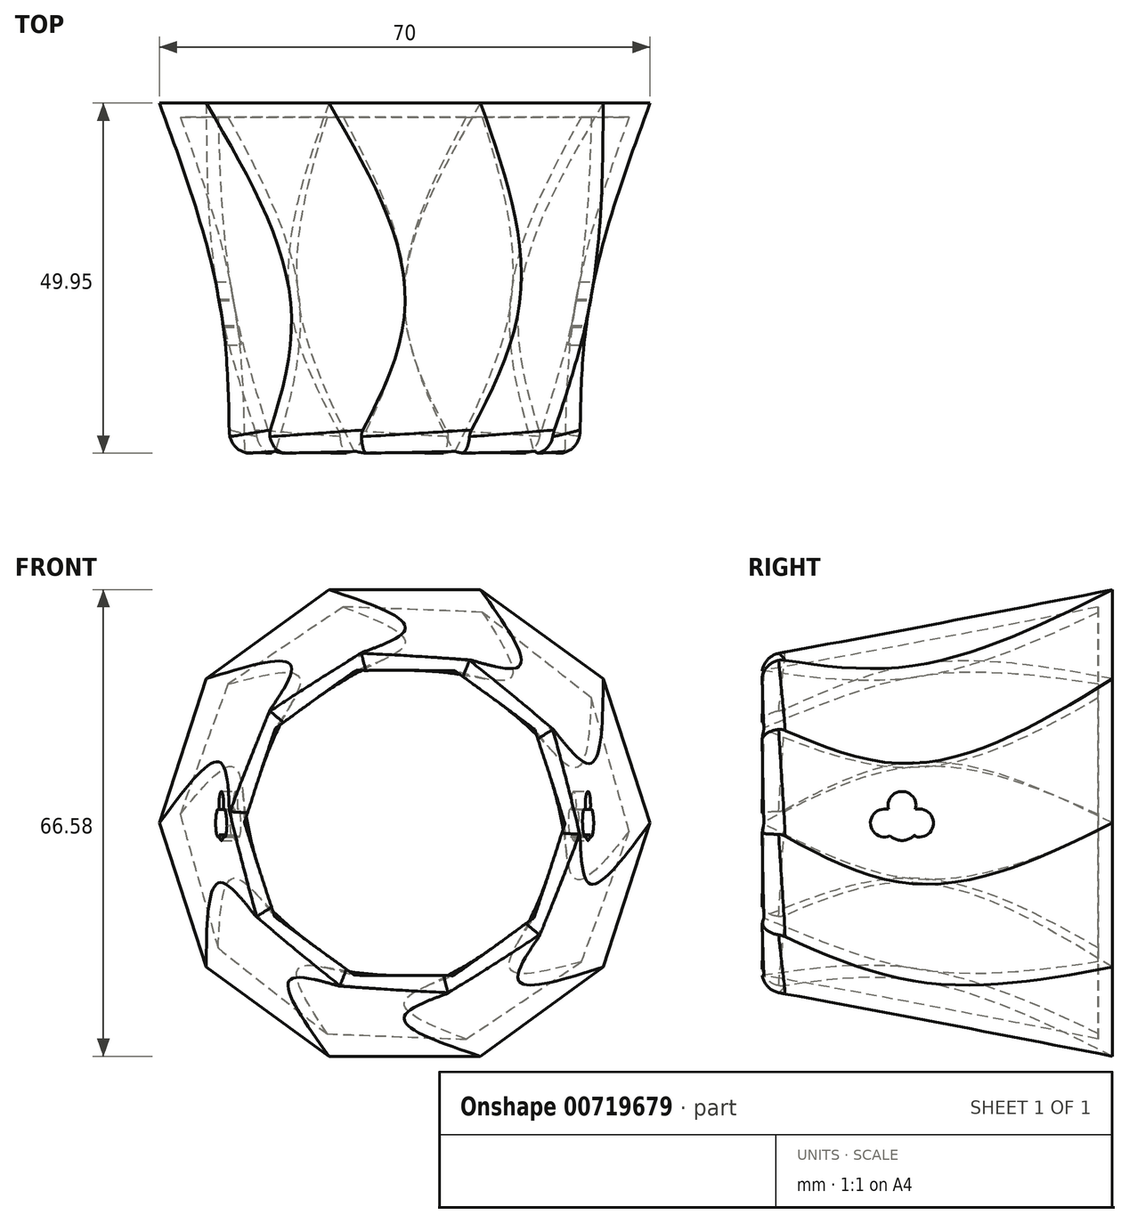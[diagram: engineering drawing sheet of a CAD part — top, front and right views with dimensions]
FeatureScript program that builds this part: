
annotation { "Feature Type Name" : "Feature", "Feature Type Description" : "" }
export const myFeature = defineFeature(function(context is Context, id is Id, definition is map)
    precondition{}
    {
        {
            var Q0;
            Q0=qCreatedBy(makeId("Front.planeOp"),FACE);
            var sketch = newSketch(context, id + "F0", { "sketchPlane" : qUnion([Q0])});
            skCircle(sketch, "E0.cCircle", {"center": v(0, 0) * mm, "radius": 35 * mm, "construction": true});
            skLineSegment(sketch, "E0.0", {"start": v(35, 0) * mm, "end": v(28.32, -20.57) * mm});
            skLineSegment(sketch, "E0.1", {"start": v(28.32, -20.57) * mm, "end": v(10.82, -33.29) * mm});
            skLineSegment(sketch, "E0.2", {"start": v(10.82, -33.29) * mm, "end": v(-10.82, -33.29) * mm});
            skLineSegment(sketch, "E0.3", {"start": v(-10.82, -33.29) * mm, "end": v(-28.32, -20.57) * mm});
            skLineSegment(sketch, "E0.4", {"start": v(-28.32, -20.57) * mm, "end": v(-35, 0) * mm});
            skLineSegment(sketch, "E0.5", {"start": v(-35, 0) * mm, "end": v(-28.32, 20.57) * mm});
            skLineSegment(sketch, "E0.6", {"start": v(-28.32, 20.57) * mm, "end": v(-10.82, 33.29) * mm});
            skLineSegment(sketch, "E0.7", {"start": v(-10.82, 33.29) * mm, "end": v(10.82, 33.29) * mm});
            skLineSegment(sketch, "E0.8", {"start": v(10.82, 33.29) * mm, "end": v(28.32, 20.57) * mm});
            skLineSegment(sketch, "E0.9", {"start": v(28.32, 20.57) * mm, "end": v(35, 0) * mm});
            skSolve(sketch);
        }
        {
            var Q0;
            Q0=qCreatedBy(makeId("Front.planeOp"),FACE);
            cPlane(context, id + "F1", {"entities" : qUnion([Q0]), "cplaneType" : CPlaneType.OFFSET, "offset" : 30 * mm, "width" : 150 * mm, "height" : 150 * mm});
        }
        {
            var Q0;
            Q0=qCreatedBy(id+"F1.planeOp",FACE);
            var sketch = newSketch(context, id + "F2", { "sketchPlane" : qUnion([Q0])});
            skCircle(sketch, "E1.cCircle", {"center": v(0, 0) * mm, "radius": 27.5 * mm, "construction": true});
            skLineSegment(sketch, "E1.0", {"start": v(-16.16, 22.25) * mm, "end": v(0, 27.5) * mm});
            skLineSegment(sketch, "E1.1", {"start": v(0, 27.5) * mm, "end": v(16.16, 22.25) * mm});
            skLineSegment(sketch, "E1.2", {"start": v(16.16, 22.25) * mm, "end": v(26.15, 8.5) * mm});
            skLineSegment(sketch, "E1.3", {"start": v(26.15, 8.5) * mm, "end": v(26.15, -8.5) * mm});
            skLineSegment(sketch, "E1.4", {"start": v(26.15, -8.5) * mm, "end": v(16.16, -22.25) * mm});
            skLineSegment(sketch, "E1.5", {"start": v(16.16, -22.25) * mm, "end": v(0, -27.5) * mm});
            skLineSegment(sketch, "E1.6", {"start": v(0, -27.5) * mm, "end": v(-16.16, -22.25) * mm});
            skLineSegment(sketch, "E1.7", {"start": v(-16.16, -22.25) * mm, "end": v(-26.15, -8.5) * mm});
            skLineSegment(sketch, "E1.8", {"start": v(-26.15, -8.5) * mm, "end": v(-26.15, 8.5) * mm});
            skLineSegment(sketch, "E1.9", {"start": v(-26.15, 8.5) * mm, "end": v(-16.16, 22.25) * mm});
            skSolve(sketch);
        }
        {
            var Q0;
            Q0=qCreatedBy(id+"F1.planeOp",FACE);
            cPlane(context, id + "F3", {"entities" : qUnion([Q0]), "cplaneType" : CPlaneType.OFFSET, "offset" : 20 * mm, "width" : 150 * mm, "height" : 150 * mm});
        }
        {
            var Q0;
            Q0=qCreatedBy(id+"F3.planeOp",FACE);
            var sketch = newSketch(context, id + "F4", { "sketchPlane" : qUnion([Q0])});
            skCircle(sketch, "E2.cCircle", {"center": v(0, 0) * mm, "radius": 25 * mm, "construction": true});
            skLineSegment(sketch, "E2.0", {"start": v(-7.73, 23.78) * mm, "end": v(7.73, 23.78) * mm});
            skLineSegment(sketch, "E2.1", {"start": v(7.73, 23.78) * mm, "end": v(20.23, 14.7) * mm});
            skLineSegment(sketch, "E2.2", {"start": v(20.23, 14.7) * mm, "end": v(25, 0) * mm});
            skLineSegment(sketch, "E2.3", {"start": v(25, 0) * mm, "end": v(20.23, -14.7) * mm});
            skLineSegment(sketch, "E2.4", {"start": v(20.23, -14.7) * mm, "end": v(7.73, -23.78) * mm});
            skLineSegment(sketch, "E2.5", {"start": v(7.73, -23.78) * mm, "end": v(-7.73, -23.78) * mm});
            skLineSegment(sketch, "E2.6", {"start": v(-7.73, -23.78) * mm, "end": v(-20.23, -14.7) * mm});
            skLineSegment(sketch, "E2.7", {"start": v(-20.23, -14.7) * mm, "end": v(-25, 0) * mm});
            skLineSegment(sketch, "E2.8", {"start": v(-25, 0) * mm, "end": v(-20.23, 14.7) * mm});
            skLineSegment(sketch, "E2.9", {"start": v(-20.23, 14.7) * mm, "end": v(-7.73, 23.78) * mm});
            skSolve(sketch);
        }
        {
            var Q0;
            Q0 = qSketchRegion(id + "F0", true);
            var Q1;
            Q1 = qSketchRegion(id + "F2", true);
            var Q2;
            Q2 = qSketchRegion(id + "F4", true);
            loft(context, id + "F5", {"sheetProfilesArray" : [{ "sheetProfileEntities" : qUnion([Q0]) }, { "sheetProfileEntities" : qUnion([Q1]) }, { "sheetProfileEntities" : qUnion([Q2]) }]});
        }
        {
            var Q0;
            Q0=makeQuery(id+"F5.opLoft","CAP_FACE",FACE,{"disambiguationData":[OSD([makeQuery(id+"F4.imprint","IMPRINT",FACE,{"disambiguationData":[TD([[makeQuery(id+"F4.imprint","IMPRINT",EDGE,{"derivedFrom":sQuery(id+"F4.wireOp",EDGE,"E2.0")}),-1.0]])]})])],"isStart":true});
            shell(context, id + "F6", {"entities" : qUnion([Q0]), "thickness" : 2 * mm});
        }
        {
            var Q0;
            Q0=makeQuery(id+"F5.opLoft","MID_CAP_EDGE",EDGE,{"disambiguationData":[OSD([sQuery(id+"F4.wireOp",EDGE,"E2.3"),sQuery(id+"F4.wireOp",EDGE,"E2.4"),sQuery(id+"F4.wireOp",EDGE,"E2.5")])],"capPos":2.0});
            var Q1;
            Q1=makeQuery(id+"F5.opLoft","MID_CAP_EDGE",EDGE,{"disambiguationData":[OSD([sQuery(id+"F4.wireOp",EDGE,"E2.4"),sQuery(id+"F4.wireOp",EDGE,"E2.5"),sQuery(id+"F4.wireOp",EDGE,"E2.6")])],"capPos":2.0});
            var Q2;
            Q2=makeQuery(id+"F5.opLoft","MID_CAP_EDGE",EDGE,{"disambiguationData":[OSD([sQuery(id+"F4.wireOp",EDGE,"E2.5"),sQuery(id+"F4.wireOp",EDGE,"E2.6"),sQuery(id+"F4.wireOp",EDGE,"E2.7")])],"capPos":2.0});
            var Q3;
            Q3=makeQuery(id+"F5.opLoft","MID_CAP_EDGE",EDGE,{"disambiguationData":[OSD([sQuery(id+"F4.wireOp",EDGE,"E2.6"),sQuery(id+"F4.wireOp",EDGE,"E2.7"),sQuery(id+"F4.wireOp",EDGE,"E2.8")])],"capPos":2.0});
            var Q4;
            Q4=makeQuery(id+"F5.opLoft","MID_CAP_EDGE",EDGE,{"disambiguationData":[OSD([sQuery(id+"F4.wireOp",EDGE,"E2.7"),sQuery(id+"F4.wireOp",EDGE,"E2.8"),sQuery(id+"F4.wireOp",EDGE,"E2.9")])],"capPos":2.0});
            var Q5;
            Q5=makeQuery(id+"F5.opLoft","MID_CAP_EDGE",EDGE,{"disambiguationData":[OSD([sQuery(id+"F4.wireOp",EDGE,"E2.0"),sQuery(id+"F4.wireOp",EDGE,"E2.8"),sQuery(id+"F4.wireOp",EDGE,"E2.9")])],"capPos":2.0});
            var Q6;
            Q6=makeQuery(id+"F5.opLoft","MID_CAP_EDGE",EDGE,{"disambiguationData":[OSD([sQuery(id+"F4.wireOp",EDGE,"E2.0"),sQuery(id+"F4.wireOp",EDGE,"E2.1"),sQuery(id+"F4.wireOp",EDGE,"E2.9")])],"capPos":2.0});
            var Q7;
            Q7=makeQuery(id+"F5.opLoft","MID_CAP_EDGE",EDGE,{"disambiguationData":[OSD([sQuery(id+"F4.wireOp",EDGE,"E2.0"),sQuery(id+"F4.wireOp",EDGE,"E2.1"),sQuery(id+"F4.wireOp",EDGE,"E2.2")])],"capPos":2.0});
            var Q8;
            Q8=makeQuery(id+"F5.opLoft","MID_CAP_EDGE",EDGE,{"disambiguationData":[OSD([sQuery(id+"F4.wireOp",EDGE,"E2.1"),sQuery(id+"F4.wireOp",EDGE,"E2.2"),sQuery(id+"F4.wireOp",EDGE,"E2.3")])],"capPos":2.0});
            var Q9;
            Q9=makeQuery(id+"F5.opLoft","MID_CAP_EDGE",EDGE,{"disambiguationData":[OSD([sQuery(id+"F4.wireOp",EDGE,"E2.2"),sQuery(id+"F4.wireOp",EDGE,"E2.3"),sQuery(id+"F4.wireOp",EDGE,"E2.4")])],"capPos":2.0});
            fillet(context, id + "F7", {"entities" : qUnion([Q0, Q1, Q2, Q3, Q4, Q5, Q6, Q7, Q8, Q9]), "radius" : 3 * mm, "tangentPropagation" : true, "allowEdgeOverflow" : false});
        }
        {
            var Q0;
            Q0=qCreatedBy(makeId("Right.planeOp"),FACE);
            var sketch = newSketch(context, id + "F8", { "sketchPlane" : qUnion([Q0])});
            skCircle(sketch, "E3", {"center": v(-30, 0) * mm, "radius": 2.5 * mm});
            skArc(sketch, "E4", {"start": v(-28.17, 1.7) * mm, "mid": v(-30, 4.5) * mm, "end": v(-31.83, 1.7) * mm});
            skArc(sketch, "E5", {"start": v(-31.7, 1.83) * mm, "mid": v(-34.5, 0) * mm, "end": v(-31.7, -1.83) * mm});
            skArc(sketch, "E6", {"start": v(-31.83, -1.7) * mm, "mid": v(-30, -4.5) * mm, "end": v(-28.17, -1.7) * mm});
            skArc(sketch, "E7", {"start": v(-28.3, -1.83) * mm, "mid": v(-25.5, 0) * mm, "end": v(-28.3, 1.83) * mm});
            skSolve(sketch);
        }
        {
            var Q0;
            Q0=makeQuery(id+"F8.imprint","IMPRINT",FACE,{"disambiguationData":[TD([[makeQuery(id+"F8.imprint","IMPRINT",EDGE,{"derivedFrom":sQuery(id+"F8.wireOp",EDGE,"E3")}),1.0]])]});
            extrude(context, id + "F9", {"entities" : qUnion([Q0]), "operationType" : NewBodyOperationType.REMOVE, "endBound" : BoundingType.SYMMETRIC, "oppositeDirection" : true, "depth" : 60 * mm, "offsetDistance" : 25 * mm});
        }
        {
            var Q0;
            {var subQ0=sQuery(id+"F8.wireOp",EDGE,"E4");var subQ1=sQuery(id+"F8.wireOp",EDGE,"E3");var subQ2=makeQuery(id+"F8.imprint","INTERSECT",VERTEX,{"disambiguationData":[OD(1.0)],"derivedFrom":[subQ1,subQ0]});Q0=makeQuery(id+"F8.imprint","IMPRINT",FACE,{"disambiguationData":[TD([[makeQuery(id+"F8.imprint","IMPRINT",EDGE,{"disambiguationData":[TD([[subQ2,-1.0]])],"derivedFrom":subQ1}),-1.0]])]});}
            var Q1;
            {var subQ0=sQuery(id+"F8.wireOp",EDGE,"E5");var subQ1=sQuery(id+"F8.wireOp",EDGE,"E3");var subQ2=makeQuery(id+"F8.imprint","INTERSECT",VERTEX,{"disambiguationData":[OD(1.0)],"derivedFrom":[subQ1,subQ0]});Q1=makeQuery(id+"F8.imprint","IMPRINT",FACE,{"disambiguationData":[TD([[makeQuery(id+"F8.imprint","IMPRINT",EDGE,{"disambiguationData":[TD([[subQ2,-1.0]])],"derivedFrom":subQ1}),-1.0]])]});}
            var Q2;
            {var subQ0=sQuery(id+"F8.wireOp",EDGE,"E5");var subQ1=sQuery(id+"F8.wireOp",EDGE,"E3");var subQ2=makeQuery(id+"F8.imprint","INTERSECT",VERTEX,{"disambiguationData":[OD(0.0)],"derivedFrom":[subQ1,subQ0]});Q2=makeQuery(id+"F8.imprint","IMPRINT",FACE,{"disambiguationData":[TD([[makeQuery(id+"F8.imprint","IMPRINT",EDGE,{"disambiguationData":[TD([[subQ2,1.0]])],"derivedFrom":subQ1}),-1.0]])]});}
            var Q3;
            {var subQ0=sQuery(id+"F8.wireOp",EDGE,"E4");var subQ1=sQuery(id+"F8.wireOp",EDGE,"E3");var subQ2=makeQuery(id+"F8.imprint","INTERSECT",VERTEX,{"disambiguationData":[OD(0.0)],"derivedFrom":[subQ1,subQ0]});Q3=makeQuery(id+"F8.imprint","IMPRINT",FACE,{"disambiguationData":[TD([[makeQuery(id+"F8.imprint","IMPRINT",EDGE,{"disambiguationData":[TD([[subQ2,1.0]])],"derivedFrom":subQ1}),-1.0]])]});}
            var Q4;
            {var subQ0=sQuery(id+"F8.wireOp",EDGE,"E5");var subQ1=sQuery(id+"F8.wireOp",EDGE,"E3");var subQ2=makeQuery(id+"F8.imprint","INTERSECT",VERTEX,{"disambiguationData":[OD(1.0)],"derivedFrom":[subQ1,subQ0]});Q4=makeQuery(id+"F8.imprint","IMPRINT",FACE,{"disambiguationData":[TD([[makeQuery(id+"F8.imprint","IMPRINT",EDGE,{"disambiguationData":[TD([[subQ2,1.0]])],"derivedFrom":subQ1}),-1.0]])]});}
            var Q5;
            {var subQ0=sQuery(id+"F8.wireOp",EDGE,"E4");var subQ1=sQuery(id+"F8.wireOp",EDGE,"E3");var subQ9=makeQuery(id+"F8.imprint","INTERSECT",VERTEX,{"disambiguationData":[OD(0.0)],"derivedFrom":[subQ1,subQ0]});Q5=makeQuery(id+"F8.imprint","IMPRINT",FACE,{"disambiguationData":[TD([[makeQuery(id+"F8.imprint","IMPRINT",EDGE,{"disambiguationData":[TD([[subQ9,-1.0]])],"derivedFrom":subQ1}),1.0]])]});}
            var Q6;
            {var subQ0=sQuery(id+"F8.wireOp",EDGE,"E6");var subQ1=sQuery(id+"F8.wireOp",EDGE,"E3");var subQ2=makeQuery(id+"F8.imprint","INTERSECT",VERTEX,{"disambiguationData":[OD(1.0)],"derivedFrom":[subQ1,subQ0]});Q6=makeQuery(id+"F8.imprint","IMPRINT",FACE,{"disambiguationData":[TD([[makeQuery(id+"F8.imprint","IMPRINT",EDGE,{"disambiguationData":[TD([[subQ2,1.0]])],"derivedFrom":subQ1}),-1.0]])]});}
            var Q7;
            {var subQ0=sQuery(id+"F8.wireOp",EDGE,"E4");var subQ1=sQuery(id+"F8.wireOp",EDGE,"E3");var subQ2=makeQuery(id+"F8.imprint","INTERSECT",VERTEX,{"disambiguationData":[OD(0.0)],"derivedFrom":[subQ1,subQ0]});Q7=makeQuery(id+"F8.imprint","IMPRINT",FACE,{"disambiguationData":[TD([[makeQuery(id+"F8.imprint","IMPRINT",EDGE,{"disambiguationData":[TD([[subQ2,-1.0]])],"derivedFrom":subQ1}),-1.0]])]});}
            var Q8;
            {var subQ0=sQuery(id+"F8.wireOp",EDGE,"E4");var subQ1=sQuery(id+"F8.wireOp",EDGE,"E3");var subQ2=makeQuery(id+"F8.imprint","INTERSECT",VERTEX,{"disambiguationData":[OD(1.0)],"derivedFrom":[subQ1,subQ0]});Q8=makeQuery(id+"F8.imprint","IMPRINT",FACE,{"disambiguationData":[TD([[makeQuery(id+"F8.imprint","IMPRINT",EDGE,{"disambiguationData":[TD([[subQ2,1.0]])],"derivedFrom":subQ1}),-1.0]])]});}
            extrude(context, id + "F10", {"entities" : qUnion([Q0, Q1, Q2, Q3, Q4, Q5, Q6, Q7, Q8]), "operationType" : NewBodyOperationType.REMOVE, "endBound" : BoundingType.SYMMETRIC, "oppositeDirection" : true, "depth" : 60 * mm, "offsetDistance" : 25 * mm});
        }
    });
